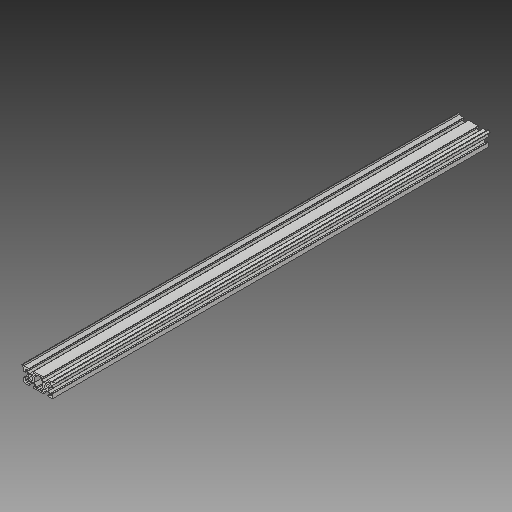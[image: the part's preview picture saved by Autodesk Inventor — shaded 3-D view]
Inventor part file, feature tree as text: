
AUTODESK INVENTOR PART (.ipt)
format: ipt  version: 2017 (Build 210142000, 142)  size: 279,552 bytes
history: native  units: mm
features: other x3, sketch x1
ambient origin geometry x8: Origin, YZ Plane, XZ Plane, XY Plane, X Axis, Y Axis, Z Axis, Center Point
bodies: Solid1 (feature_tree)
feature tree (4):
  other  "Makerslide 600mm.ipt"
  other  "Solid1::Makerslide 600mm.ipt"
  other  "TaggingFeature1"
  sketch  "Sketch1"  dims[d0=10.0mm]
